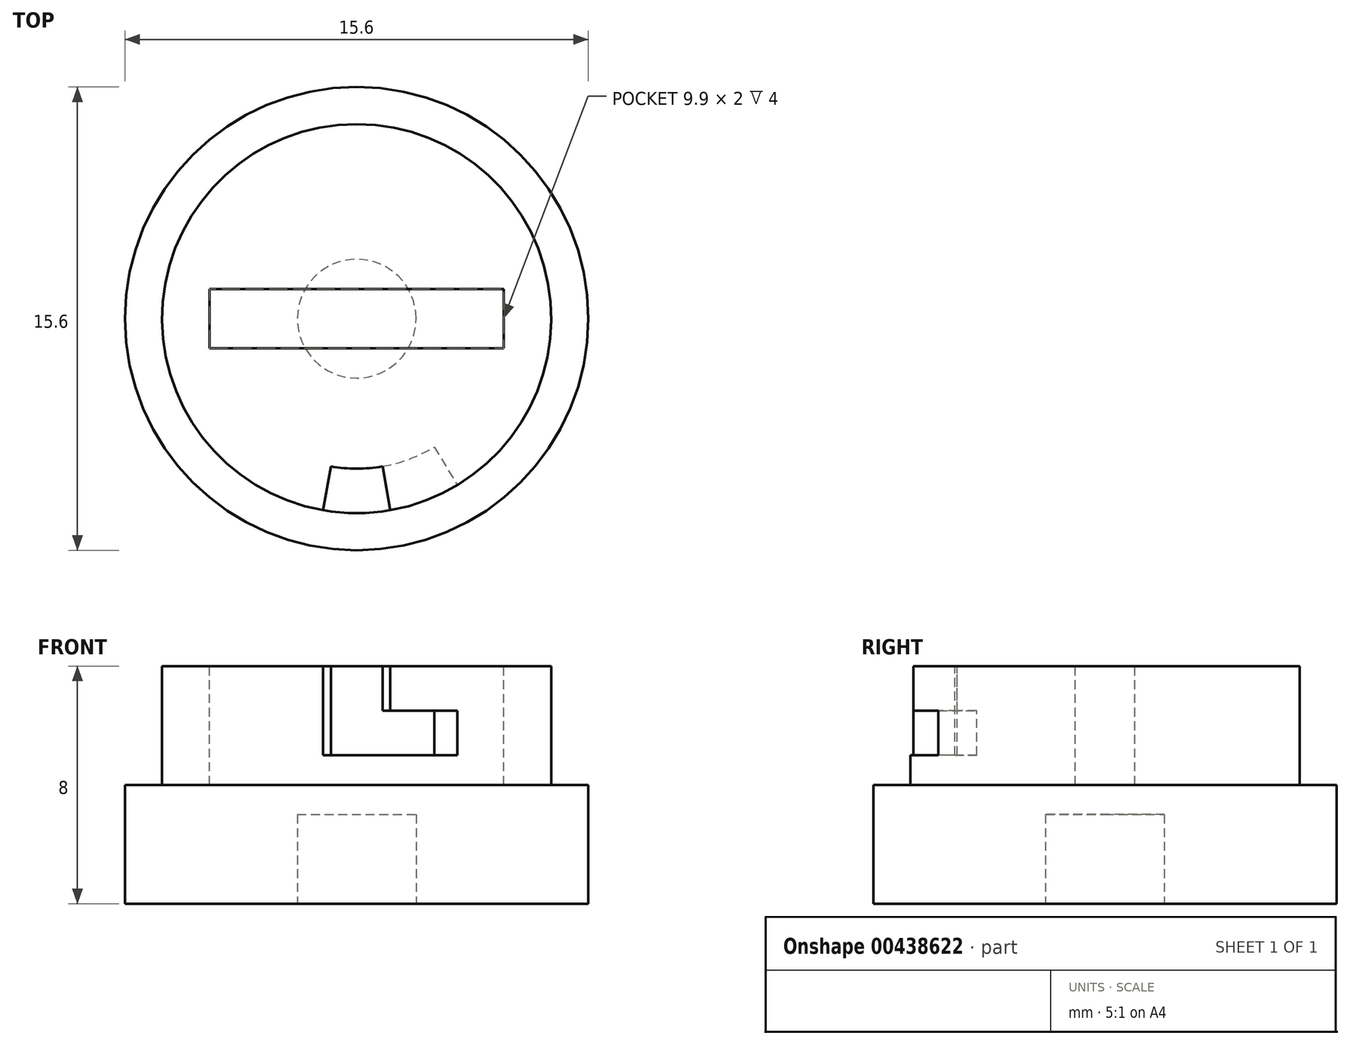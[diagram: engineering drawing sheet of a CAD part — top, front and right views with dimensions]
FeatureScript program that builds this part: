
annotation { "Feature Type Name" : "Feature", "Feature Type Description" : "" }
export const myFeature = defineFeature(function(context is Context, id is Id, definition is map)
    precondition{}
    {
        {
            var Q0;
            Q0=qCreatedBy(makeId("Top.planeOp"),FACE);
            var sketch = newSketch(context, id + "F0", { "sketchPlane" : qUnion([Q0])});
            skCircle(sketch, "E0", {"center": v(0, 0) * mm, "radius": 7.8 * mm});
            skSolve(sketch);
        }
        {
            var Q0;
            Q0 = qSketchRegion(id + "F0", true);
            extrude(context, id + "F1", {"entities" : qUnion([Q0]), "depth" : 4 * mm});
        }
        {
            var Q0;
            Q0=makeQuery(id+"F1.opExtrude","CAP_FACE",FACE,{"disambiguationData":[OSD([sQuery(id+"F0.wireOp",EDGE,"E0"),sQuery(id+"F0.wireOp",EDGE,"6HcKctP9-Frpi-ehtU-NWM4-VYv9y4EvmBGS")])],"isStart":false});
            var sketch = newSketch(context, id + "F2", { "sketchPlane" : qUnion([Q0])});
            skCircle(sketch, "E1", {"center": v(0, 0) * mm, "radius": 6.55 * mm});
            skSolve(sketch);
        }
        {
            var Q0;
            Q0 = qSketchRegion(id + "F2", true);
            extrude(context, id + "F3", {"entities" : qUnion([Q0]), "operationType" : NewBodyOperationType.ADD, "depth" : 4 * mm});
        }
        {
            var Q0;
            Q0=makeQuery(id+"F3.opExtrude","CAP_FACE",FACE,{"disambiguationData":[OSD([sQuery(id+"F2.wireOp",EDGE,"E1")])],"isStart":false});
            var sketch = newSketch(context, id + "F4", { "sketchPlane" : qUnion([Q0])});
            skLineSegment(sketch, "E2.bottom", {"start": v(4.95, 1) * mm, "end": v(-4.95, 1) * mm});
            skLineSegment(sketch, "E2.top", {"start": v(4.95, -1) * mm, "end": v(-4.95, -1) * mm});
            skLineSegment(sketch, "E2.left", {"start": v(4.95, 1) * mm, "end": v(4.95, -1) * mm});
            skLineSegment(sketch, "E2.right", {"start": v(-4.95, 1) * mm, "end": v(-4.95, -1) * mm});
            skPoint(sketch, "E2.middle", {"position": v(0, 0) * mm});
            skSolve(sketch);
        }
        {
            var Q0;
            Q0=makeQuery(id+"F4.imprint","IMPRINT",FACE,{"disambiguationData":[TD([[makeQuery(id+"F4.imprint","IMPRINT",EDGE,{"derivedFrom":sQuery(id+"F4.wireOp",EDGE,"E2.bottom")}),1.0]])]});
            extrude(context, id + "F5", {"entities" : qUnion([Q0]), "operationType" : NewBodyOperationType.REMOVE, "oppositeDirection" : true, "depth" : 4 * mm});
        }
        {
            var Q0;
            Q0=makeQuery(id+"F3.opExtrude","CAP_FACE",FACE,{"disambiguationData":[OSD([sQuery(id+"F2.wireOp",EDGE,"E1")])],"isStart":false});
            cPlane(context, id + "F6", {"entities" : qUnion([Q0]), "cplaneType" : CPlaneType.OFFSET, "offset" : 2.25 * mm, "oppositeDirection" : true, "width" : 150 * mm, "height" : 150 * mm});
        }
        {
            var Q0;
            Q0=qCreatedBy(makeId("Right.planeOp"),FACE);
            var sketch = newSketch(context, id + "F7", { "sketchPlane" : qUnion([Q0])});
            skLineSegment(sketch, "E3.bottom", {"start": v(-5.05, 6.5) * mm, "end": v(-6.55, 6.5) * mm});
            skLineSegment(sketch, "E3.top", {"start": v(-5.05, 8) * mm, "end": v(-6.55, 8) * mm});
            skLineSegment(sketch, "E3.left", {"start": v(-5.05, 6.5) * mm, "end": v(-5.05, 8) * mm});
            skLineSegment(sketch, "E3.right", {"start": v(-6.55, 6.5) * mm, "end": v(-6.55, 8) * mm});
            skSolve(sketch);
        }
        {
            var Q0;
            Q0=qCreatedBy(id+"F6.planeOp",FACE);
            var sketch = newSketch(context, id + "F8", { "sketchPlane" : qUnion([Q0])});
            skArc(sketch, "E4", {"start": v(0, -5.8) * mm, "mid": v(1.56, -5.59) * mm, "end": v(3, -4.96) * mm});
            skSolve(sketch);
        }
        {
            var Q0;
            Q0=makeQuery(id+"F3.opExtrude","CAP_FACE",FACE,{"disambiguationData":[OSD([sQuery(id+"F2.wireOp",EDGE,"E1")])],"isStart":false});
            cPlane(context, id + "F9", {"entities" : qUnion([Q0]), "cplaneType" : CPlaneType.OFFSET, "offset" : 0.75 * mm, "oppositeDirection" : true, "width" : 150 * mm, "height" : 150 * mm});
        }
        {
            var Q0;
            Q0=qCreatedBy(id+"F9.planeOp",FACE);
            var sketch = newSketch(context, id + "F10", { "sketchPlane" : qUnion([Q0])});
            skArc(sketch, "E5", {"start": v(0, -5.8) * mm, "mid": v(0.5, -5.78) * mm, "end": v(1, -5.71) * mm});
            skArc(sketch, "E6.MirrorCS", {"start": v(0, -5.8) * mm, "mid": v(-0.5, -5.78) * mm, "end": v(-1, -5.71) * mm});
            skSolve(sketch);
        }
        {
            var Q0;
            Q0 = qSketchRegion(id + "F7", true);
            var Q1;
            Q1=sQuery(id+"F10.wireOp",EDGE,"E5");
            sweep(context, id + "F11", {"operationType" : NewBodyOperationType.REMOVE, "profiles" : qUnion([Q0]), "path" : qUnion([Q1])});
        }
        {
            var Q0;
            Q0=makeQuery(id+"F11.boolean.opBoolean","COPY",FACE,{"derivedFrom":makeQuery(id+"F11.opSweep","CAP_FACE",FACE,{"disambiguationData":[OSD([sQuery(id+"F7.wireOp",EDGE,"E3.bottom"),sQuery(id+"F7.wireOp",EDGE,"E3.top"),sQuery(id+"F7.wireOp",EDGE,"E3.left"),sQuery(id+"F7.wireOp",EDGE,"E3.right"),sQuery(id+"F10.wireOp",VERTEX,"E5.start")])],"isStart":true})});
            var Q1;
            Q1=sQuery(id+"F10.wireOp",EDGE,"E6.MirrorCS");
            sweep(context, id + "F12", {"operationType" : NewBodyOperationType.REMOVE, "profiles" : qUnion([Q0]), "path" : qUnion([Q1])});
        }
        {
            var Q0;
            {var subQ0=sQuery(id+"F7.wireOp",EDGE,"E3.bottom");Q0=makeQuery(id+"F12.boolean.opBoolean","MERGE",FACE,{"derivedFrom":[makeQuery(id+"F11.boolean.opBoolean","COPY",FACE,{"derivedFrom":makeQuery(id+"F11.opSweep","SWEPT_FACE",FACE,{"disambiguationData":[OSD([subQ0,sQuery(id+"F10.wireOp",EDGE,"E5")])]})}),makeQuery(id+"F12.opSweep","SWEPT_FACE",FACE,{"disambiguationData":[OSD([subQ0,sQuery(id+"F10.wireOp",VERTEX,"E5.start"),sQuery(id+"F10.wireOp",EDGE,"E6.MirrorCS")])]})]});}
            extrude(context, id + "F13", {"entities" : qUnion([Q0]), "operationType" : NewBodyOperationType.REMOVE, "oppositeDirection" : true, "depth" : 1.5 * mm});
        }
        {
            var Q0;
            {var subQ0=sQuery(id+"F10.wireOp",VERTEX,"E5.end");var subQ1=sQuery(id+"F7.wireOp",EDGE,"E3.bottom");Q0=makeQuery(id+"F13.boolean.opBoolean","MERGE",FACE,{"derivedFrom":[makeQuery(id+"F11.boolean.opBoolean","COPY",FACE,{"derivedFrom":makeQuery(id+"F11.opSweep","CAP_FACE",FACE,{"disambiguationData":[OSD([subQ1,sQuery(id+"F7.wireOp",EDGE,"E3.top"),sQuery(id+"F7.wireOp",EDGE,"E3.left"),sQuery(id+"F7.wireOp",EDGE,"E3.right"),subQ0])],"isStart":false})}),makeQuery(id+"F13.opExtrude","SWEPT_FACE",FACE,{"disambiguationData":[OSD([subQ1,subQ0])]})]});}
            var sketch = newSketch(context, id + "F14", { "sketchPlane" : qUnion([Q0])});
            skLineSegment(sketch, "E7.bottom", {"start": v(6.55, 5) * mm, "end": v(5.05, 5) * mm});
            skLineSegment(sketch, "E7.top", {"start": v(6.55, 6.5) * mm, "end": v(5.05, 6.5) * mm});
            skLineSegment(sketch, "E7.left", {"start": v(6.55, 5) * mm, "end": v(6.55, 6.5) * mm});
            skLineSegment(sketch, "E7.right", {"start": v(5.05, 5) * mm, "end": v(5.05, 6.5) * mm});
            skSolve(sketch);
        }
        {
            var Q0;
            Q0=makeQuery(id+"F14.imprint","IMPRINT",FACE,{"disambiguationData":[TD([[makeQuery(id+"F14.imprint","IMPRINT",EDGE,{"derivedFrom":sQuery(id+"F14.wireOp",EDGE,"E7.bottom")}),-1.0]])]});
            var Q1;
            Q1=sQuery(id+"F8.wireOp",EDGE,"E4");
            sweep(context, id + "F15", {"operationType" : NewBodyOperationType.REMOVE, "profiles" : qUnion([Q0]), "path" : qUnion([Q1])});
        }
        {
            var Q0;
            Q0=makeQuery(id+"F1.opExtrude","CAP_FACE",FACE,{"disambiguationData":[OSD([sQuery(id+"F0.wireOp",EDGE,"E0")])],"isStart":true});
            var sketch = newSketch(context, id + "F16", { "sketchPlane" : qUnion([Q0])});
            skCircle(sketch, "E8", {"center": v(0, 0) * mm, "radius": 2 * mm});
            skSolve(sketch);
        }
        {
            var Q0;
            Q0 = qSketchRegion(id + "F16", true);
            extrude(context, id + "F17", {"entities" : qUnion([Q0]), "operationType" : NewBodyOperationType.REMOVE, "oppositeDirection" : true, "depth" : 3 * mm});
        }
    });
